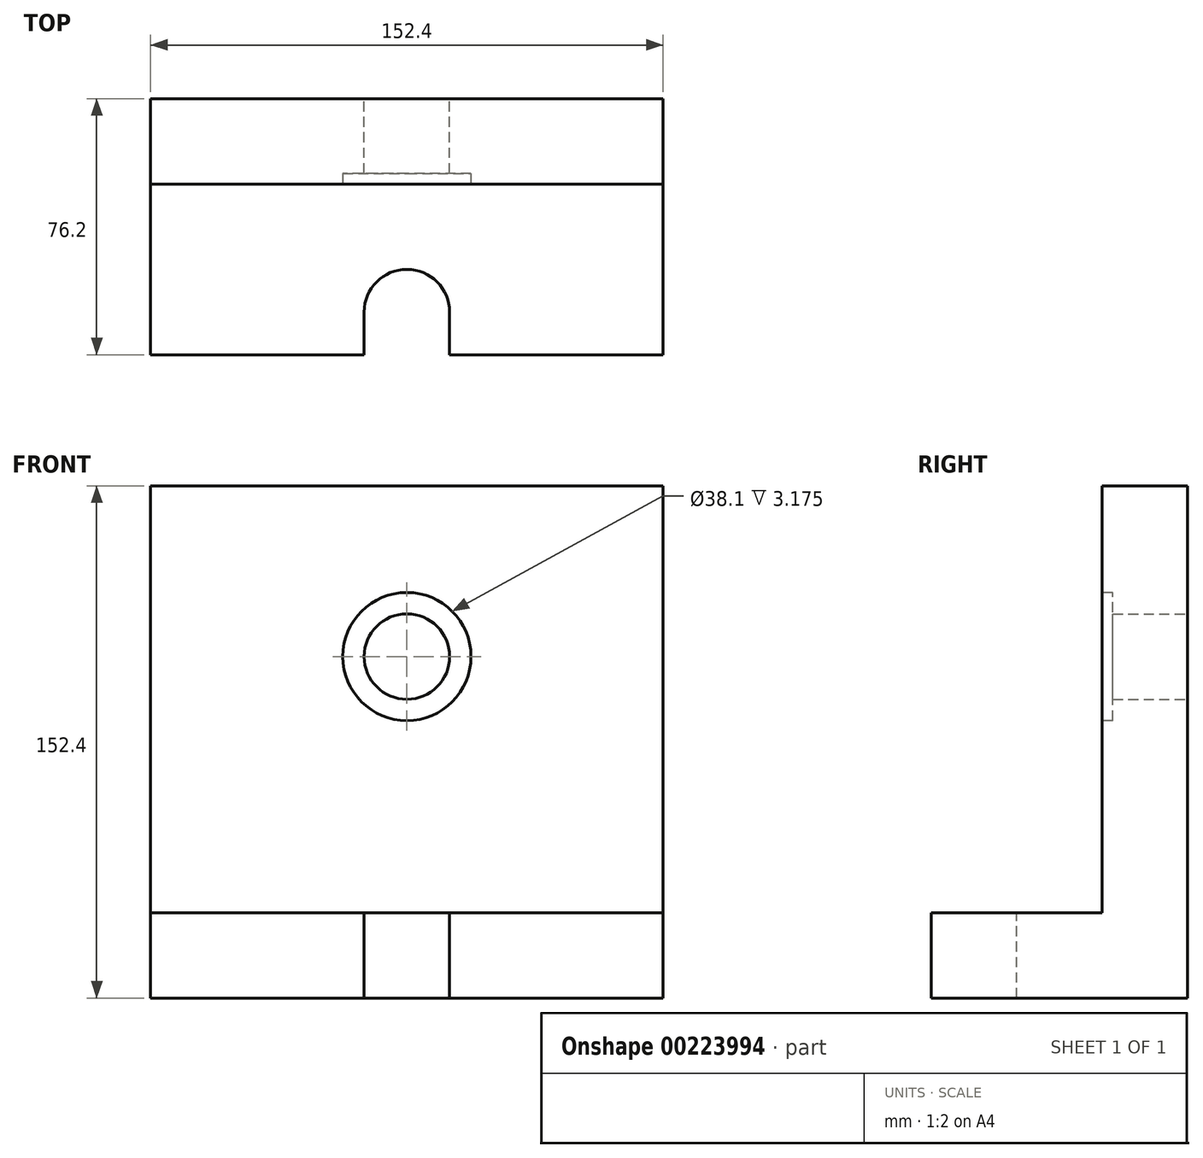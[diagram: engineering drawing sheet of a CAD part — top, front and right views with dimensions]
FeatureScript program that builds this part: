
annotation { "Feature Type Name" : "Feature", "Feature Type Description" : "" }
export const myFeature = defineFeature(function(context is Context, id is Id, definition is map)
    precondition{}
    {
        {
            var Q0;
            Q0=qCreatedBy(makeId("Right.planeOp"),FACE);
            var sketch = newSketch(context, id + "F0", { "sketchPlane" : qUnion([Q0])});
            skLineSegment(sketch, "E0", {"start": v(0, 0) * mm, "end": v(-76.2, 0) * mm});
            skLineSegment(sketch, "E1", {"start": v(-76.2, 0) * mm, "end": v(-76.2, 25.4) * mm});
            skLineSegment(sketch, "E2", {"start": v(-76.2, 25.4) * mm, "end": v(-25.4, 25.4) * mm});
            skLineSegment(sketch, "E3", {"start": v(-25.4, 25.4) * mm, "end": v(-25.4, 152.4) * mm});
            skLineSegment(sketch, "E4", {"start": v(-25.4, 152.4) * mm, "end": v(0, 152.4) * mm});
            skLineSegment(sketch, "E5", {"start": v(0, 152.4) * mm, "end": v(0, 0) * mm});
            skSolve(sketch);
        }
        {
            var Q0;
            Q0=makeQuery(id+"F0.imprint","IMPRINT",FACE,{"disambiguationData":[TD([[makeQuery(id+"F0.imprint","IMPRINT",EDGE,{"derivedFrom":sQuery(id+"F0.wireOp",EDGE,"E0")}),-1.0]])]});
            extrude(context, id + "F1", {"entities" : qUnion([Q0]), "endBound" : BoundingType.SYMMETRIC, "depth" : 152.4 * mm});
        }
        {
            var Q0;
            Q0=makeQuery(id+"F1.opExtrude","SWEPT_FACE",FACE,{"disambiguationData":[OSD([sQuery(id+"F0.wireOp",EDGE,"E5")])]});
            var sketch = newSketch(context, id + "F2", { "sketchPlane" : qUnion([Q0])});
            skCircle(sketch, "E6", {"center": v(0, 101.6) * mm, "radius": 12.7 * mm});
            skSolve(sketch);
        }
        {
            var Q0;
            Q0=makeQuery(id+"F2.imprint","IMPRINT",FACE,{"disambiguationData":[TD([[makeQuery(id+"F2.imprint","IMPRINT",EDGE,{"derivedFrom":sQuery(id+"F2.wireOp",EDGE,"E6")}),1.0]])]});
            extrude(context, id + "F3", {"entities" : qUnion([Q0]), "operationType" : NewBodyOperationType.REMOVE, "endBound" : BoundingType.THROUGH_ALL, "oppositeDirection" : true, "depth" : 25.4 * mm});
        }
        {
            var Q0;
            Q0=makeQuery(id+"F1.opExtrude","SWEPT_FACE",FACE,{"disambiguationData":[OSD([sQuery(id+"F0.wireOp",EDGE,"E2")])]});
            var sketch = newSketch(context, id + "F4", { "sketchPlane" : qUnion([Q0])});
            skLineSegment(sketch, "E7", {"start": v(-12.7, -76.2) * mm, "end": v(-12.7, -63.5) * mm});
            skLineSegment(sketch, "E8", {"start": v(12.7, -63.5) * mm, "end": v(12.7, -76.2) * mm});
            skArc(sketch, "E9", {"start": v(12.7, -63.5) * mm, "mid": v(0, -50.8) * mm, "end": v(-12.7, -63.5) * mm});
            skSolve(sketch);
        }
        {
            var Q0;
            {var subQ0=sQuery(id+"F4.wireOp",EDGE,"E7");Q0=makeQuery(id+"F4.imprint","IMPRINT",FACE,{"disambiguationData":[TD([[makeQuery(id+"F4.imprint","IMPRINT",EDGE,{"derivedFrom":subQ0}),-1.0]])]});}
            extrude(context, id + "F5", {"entities" : qUnion([Q0]), "operationType" : NewBodyOperationType.REMOVE, "endBound" : BoundingType.THROUGH_ALL, "oppositeDirection" : true, "depth" : 25.4 * mm});
        }
        {
            var Q0;
            Q0=makeQuery(id+"F1.opExtrude","SWEPT_FACE",FACE,{"disambiguationData":[OSD([sQuery(id+"F0.wireOp",EDGE,"E3")])]});
            var sketch = newSketch(context, id + "F6", { "sketchPlane" : qUnion([Q0])});
            skCircle(sketch, "E10", {"center": v(0, 101.6) * mm, "radius": 19.05 * mm});
            skSolve(sketch);
        }
        {
            var Q0;
            Q0=makeQuery(id+"F6.imprint","IMPRINT",FACE,{"disambiguationData":[TD([[makeQuery(id+"F6.imprint","IMPRINT",EDGE,{"derivedFrom":sQuery(id+"F6.wireOp",EDGE,"E10")}),1.0]])]});
            extrude(context, id + "F7", {"entities" : qUnion([Q0]), "operationType" : NewBodyOperationType.REMOVE, "endBound" : BoundingType.SYMMETRIC, "oppositeDirection" : true, "depth" : 6.35 * mm});
        }
    });
